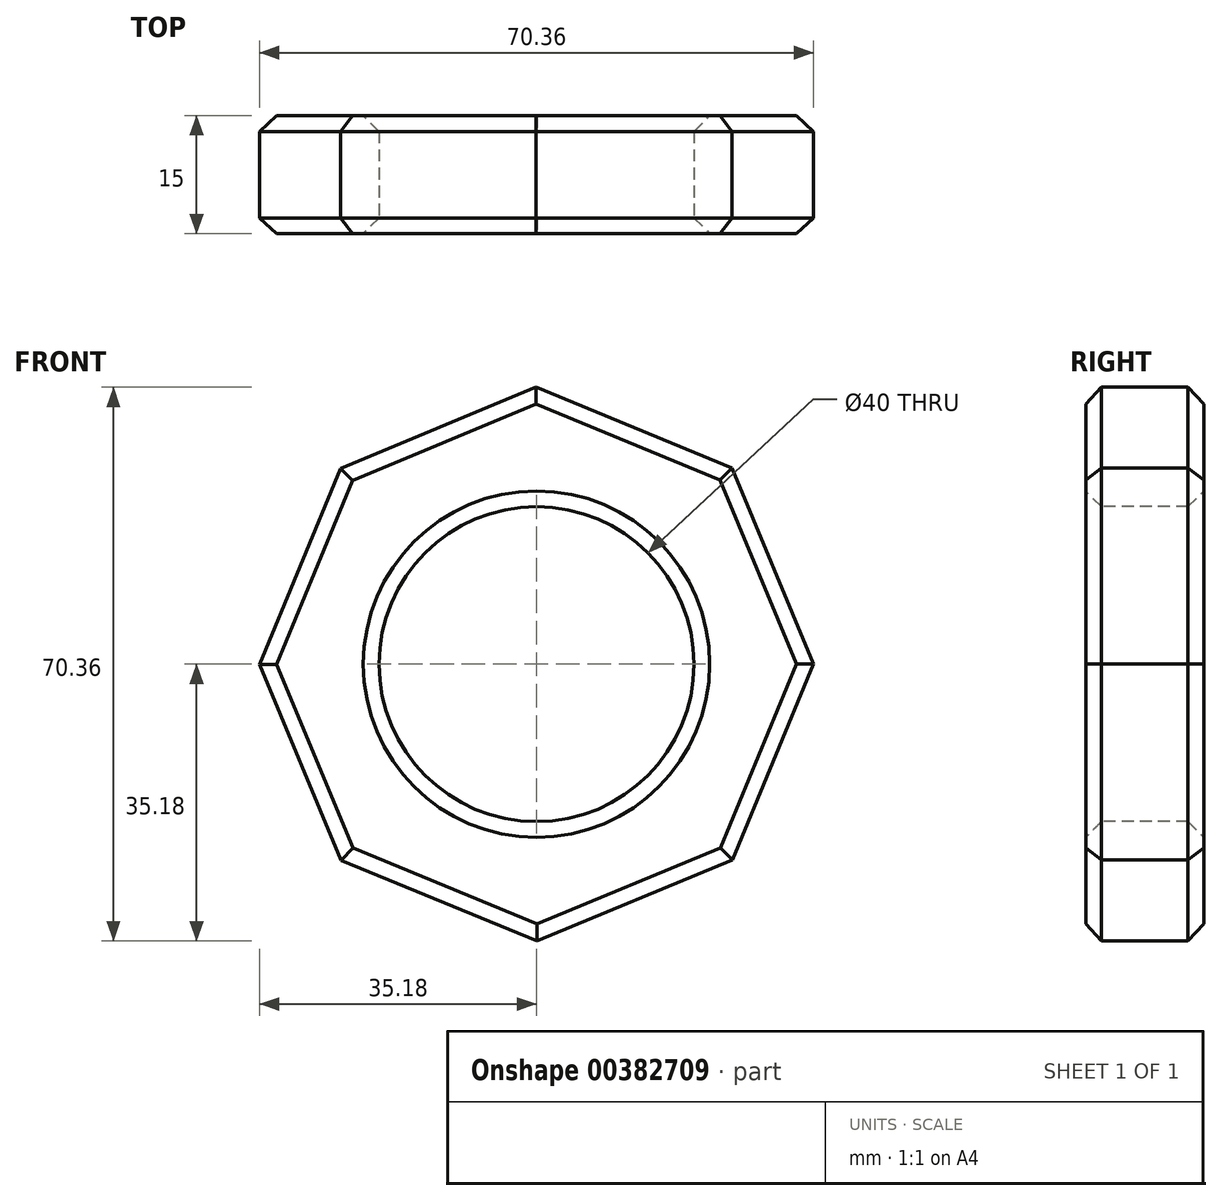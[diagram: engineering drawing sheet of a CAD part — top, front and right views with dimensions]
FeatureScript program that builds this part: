
annotation { "Feature Type Name" : "Feature", "Feature Type Description" : "" }
export const myFeature = defineFeature(function(context is Context, id is Id, definition is map)
    precondition{}
    {
        {
            var Q0;
            Q0=qCreatedBy(makeId("Front.planeOp"),FACE);
            var sketch = newSketch(context, id + "F0", { "sketchPlane" : qUnion([Q0])});
            skCircle(sketch, "E0.cCircle", {"center": v(0, 0) * mm, "radius": 32.5 * mm, "construction": true});
            skLineSegment(sketch, "E0.0", {"start": v(-0.04, 35.18) * mm, "end": v(24.84, 24.9) * mm});
            skLineSegment(sketch, "E0.1", {"start": v(24.84, 24.9) * mm, "end": v(35.18, 0.04) * mm});
            skLineSegment(sketch, "E0.2", {"start": v(35.18, 0.04) * mm, "end": v(24.9, -24.84) * mm});
            skLineSegment(sketch, "E0.3", {"start": v(24.9, -24.84) * mm, "end": v(0.04, -35.18) * mm});
            skLineSegment(sketch, "E0.4", {"start": v(0.04, -35.18) * mm, "end": v(-24.84, -24.9) * mm});
            skLineSegment(sketch, "E0.5", {"start": v(-24.84, -24.9) * mm, "end": v(-35.18, -0.04) * mm});
            skLineSegment(sketch, "E0.6", {"start": v(-35.18, -0.04) * mm, "end": v(-24.9, 24.84) * mm});
            skLineSegment(sketch, "E0.7", {"start": v(-24.9, 24.84) * mm, "end": v(-0.04, 35.18) * mm});
            skPoint(sketch, "E0.0.midPoint", {"position": v(12.4, 30.04) * mm});
            skSolve(sketch);
        }
        {
            var Q0;
            Q0=makeQuery(id+"F0.imprint","IMPRINT",FACE,{"disambiguationData":[TD([[makeQuery(id+"F0.imprint","IMPRINT",EDGE,{"derivedFrom":sQuery(id+"F0.wireOp",EDGE,"E0.0")}),-1.0]])]});
            extrude(context, id + "F1", {"entities" : qUnion([Q0]), "depth" : 15 * mm});
        }
        {
            var Q0;
            Q0=makeQuery(id+"F1.opExtrude","CAP_FACE",FACE,{"disambiguationData":[OSD([sQuery(id+"F0.wireOp",EDGE,"E0.0"),sQuery(id+"F0.wireOp",EDGE,"E0.1"),sQuery(id+"F0.wireOp",EDGE,"E0.2"),sQuery(id+"F0.wireOp",EDGE,"E0.3"),sQuery(id+"F0.wireOp",EDGE,"E0.4"),sQuery(id+"F0.wireOp",EDGE,"E0.5"),sQuery(id+"F0.wireOp",EDGE,"E0.6"),sQuery(id+"F0.wireOp",EDGE,"E0.7")])],"isStart":false});
            var sketch = newSketch(context, id + "F2", { "sketchPlane" : qUnion([Q0])});
            skCircle(sketch, "E1", {"center": v(0, 0) * mm, "radius": 20 * mm});
            skSolve(sketch);
        }
        {
            var Q0;
            Q0 = qSketchRegion(id + "F2", true);
            extrude(context, id + "F3", {"entities" : qUnion([Q0]), "operationType" : NewBodyOperationType.REMOVE, "oppositeDirection" : true, "depth" : 25 * mm});
        }
        {
            var Q0;
            Q0=makeQuery(id+"F1.opExtrude","CAP_FACE",FACE,{"disambiguationData":[OSD([sQuery(id+"F0.wireOp",EDGE,"E0.0"),sQuery(id+"F0.wireOp",EDGE,"E0.1"),sQuery(id+"F0.wireOp",EDGE,"E0.2"),sQuery(id+"F0.wireOp",EDGE,"E0.3"),sQuery(id+"F0.wireOp",EDGE,"E0.4"),sQuery(id+"F0.wireOp",EDGE,"E0.5"),sQuery(id+"F0.wireOp",EDGE,"E0.6"),sQuery(id+"F0.wireOp",EDGE,"E0.7")])],"isStart":false});
            var Q1;
            Q1=makeQuery(id+"F1.opExtrude","CAP_FACE",FACE,{"disambiguationData":[OSD([sQuery(id+"F0.wireOp",EDGE,"E0.0"),sQuery(id+"F0.wireOp",EDGE,"E0.1"),sQuery(id+"F0.wireOp",EDGE,"E0.2"),sQuery(id+"F0.wireOp",EDGE,"E0.3"),sQuery(id+"F0.wireOp",EDGE,"E0.4"),sQuery(id+"F0.wireOp",EDGE,"E0.5"),sQuery(id+"F0.wireOp",EDGE,"E0.6"),sQuery(id+"F0.wireOp",EDGE,"E0.7")])],"isStart":true});
            chamfer(context, id + "F4", {"entities" : qUnion([Q0, Q1]), "width" : 2 * mm, "tangentPropagation" : true});
        }
    });
